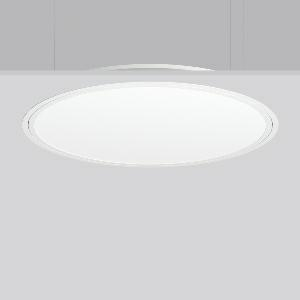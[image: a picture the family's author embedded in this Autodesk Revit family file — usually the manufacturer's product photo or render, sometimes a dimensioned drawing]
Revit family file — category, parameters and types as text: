
# Revit family: triona_round_e_312387_002_1_12_b85f
name_source: partatom
category: Lighting Fixtures
units: mm (PartAtom-declared; Revit-internal decimal feet)

## family parameters
Cut with Voids When Loaded = No
Host = Face
Light Source = No
Part Type = Normal
Room Calculation Point = No
Round Connector Dimension = Use Diameter
Shared = No

## types (1)
- TRIONA round E (1 x LED Modul 840, 8300 lm, 4000)
    Apparent Load = 80 VA
    CIE Flux Codes = 49 80 96 100 100
    Color Rendering = 80
    Color Temperature = 4000
    Default Elevation = 1800 mm
    Description = Series: TRIONA round
Decorative round LED recessed surface luminaire. Cover made of sheet steel, powder-coated. Frame made of aluminium, powder-coated. Recessed ring: aluminium extrusion profile, powder coated. Light emission through a diffuser: plastic, opal. Lightguide and diffuser made of non-yellowing plastic (PMMA). Lateral light emission (RZB SIDELITE technology) for above-average homogeneous light distribution. Suitable for installation in cavity ceilings. Tool-free mounting system thanks to the rocker arm mechanism (patent pending). Electronic ballast included. Very easy installation thanks to Plug+Play connection. 
Colour: traffic white, matt (RAL 9016)
Diameter: 889 mm
Height: 2 mm
Cut-out diameter: 866 mm
Recess height: 100 mm
Luminaire: recess height: 89 mm
Lamp: LED
Socket: without socket
Colour temperature: 4000K
Colour rendering index (CRI): 80
System power: 80 W
Rated luminous flux: 8300 lm
Luminous efficiency: 104 lm/W
Control gear: Converter, dimmable, DALI
Protection class: I
Type of protection: IP 40
    Height = 0 mm  [stored 0 ft]
    Lamp = 1 x LED Modul 840
    Lamp Light Flux = 8300 lm
    Lamp count = 1
    Length = 889 mm
    Lifetime = 50000 h
    Luminous efficacy = 104 lm/W
    Manufacturer = RZB
    ModVariant = No
    Model = 312387.002.1.12
    Mounting Place = Ceiling
    Mounting Type = Recessed
    Number of Poles = 1
    OnlyDefault = Yes
    Power Factor = 1
    Product Name = TRIONA round E
    Product group = Recessed modular luminaires
    ProductGroupID = 406
    Protection Class = Protection class I
    Protection Degree = IP 20
    RLX_Detail_Level = 1
    RLX_Emergency_Light_Flux = 0 lm
    RLX_Emergency_Type = 0
    RLX_Emergency_Type_DB = No
    RlxData = <blob elided: 37825 chars, md5=b0f8d2d0>
    Socket = socket
    Standby Power = 0 W
    System Light Flux = 8300 lm
    System Power = 80 W
    Type Comments = Product without accessories
    Type Image = 312387.002.12.jpg
    URL = http://relux.com
    VarID = ---
    Voltage = 230 V
    Voltage Range = 220-240 V
    Weight = 0.00 kg
    Width = 0 mm  [stored 0 ft]

note: [stored X ft] marks values corroborated as IEEE doubles in the binary element streams (Revit-internal decimal feet)

## geometry (parser evidence)
native form markers: Blend x4, Sweep x9
no freeform markers — native parametric forms only
